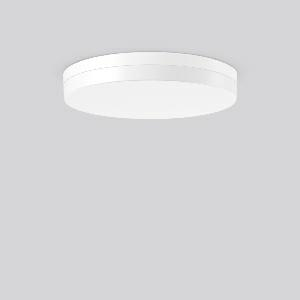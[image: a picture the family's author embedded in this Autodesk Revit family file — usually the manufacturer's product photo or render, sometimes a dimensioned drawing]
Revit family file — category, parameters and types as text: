
# Revit family: flat_slim_round_312633_002_730_d5c7
name_source: partatom
category: Lighting Fixtures
units: mm (PartAtom-declared; Revit-internal decimal feet)

## family parameters
Cut with Voids When Loaded = No
Host = Face
Light Source = No
Part Type = Normal
Room Calculation Point = No
Round Connector Dimension = Use Diameter
Shared = No

## types (1)
- MultiLumen 1 830 (1 x LED Modul 830, 3350 lm, 3000)
    Apparent Load = 31 VA
    CIE Flux Codes = 41 71 90 86 100
    Color Rendering = 80
    Color Temperature = 3000
    Default Elevation = 1800 mm
    Height = 75 mm
    Lamp = 1 x LED Modul 830
    Lamp Light Flux = 3350 lm
    Lamp count = 1
    Length = 480 mm
    Lifetime = 50000 h
    Luminous efficacy = 108 lm/W
    Manufacturer = RZB
    ModVariant = No
    Model = 312633.002.730
    Mounting Place = Ceiling
    Mounting Type = Surface mounted
    Number of Poles = 1
    OnlyDefault = Yes
    Power Factor = 1
    Product Name = FLAT SLIM round
    Product group = Surface mounted ceiling and wall luminaires
    ProductGroupID = 305
    Protection Class = Protection class I
    Protection Degree = Degree of protection
    RLX_Detail_Level = 1
    RLX_Emergency_Light_Flux = 0 lm
    RLX_Emergency_Type = 0
    RLX_Emergency_Type_DB = No
    RlxData = <blob elided: 21385 chars, md5=3ee9681b>
    Socket = socket
    Standby Power = 0 W
    System Light Flux = 3350 lm
    System Power = 31 W
    Type Comments = MultiLumen 1 830
    Type Image = 312633.002.jpg
    URL = http://relux.com
    VarID = multilumen_1_830
    Voltage = 0 V
    Weight = 0.00 kg
    Width = 0 mm  [stored 0 ft]

note: [stored X ft] marks values corroborated as IEEE doubles in the binary element streams (Revit-internal decimal feet)

## geometry (parser evidence)
native form markers: Blend x4, Sweep x15
no freeform markers — native parametric forms only
